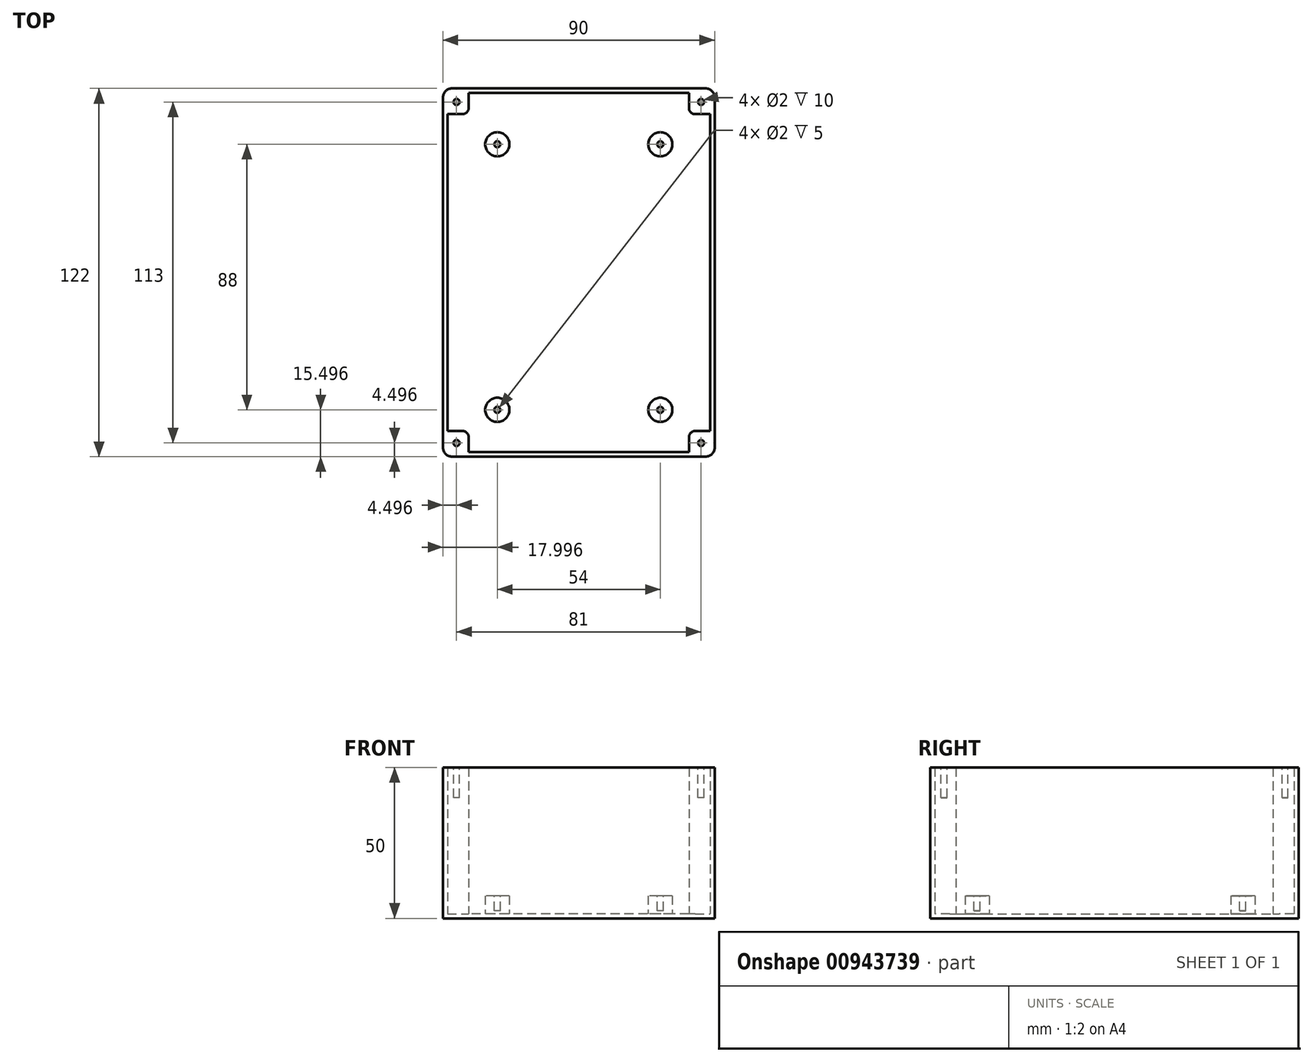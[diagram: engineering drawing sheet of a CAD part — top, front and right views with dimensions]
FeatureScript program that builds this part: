
annotation { "Feature Type Name" : "Feature", "Feature Type Description" : "" }
export const myFeature = defineFeature(function(context is Context, id is Id, definition is map)
    precondition{}
    {
        {
            var Q0;
            Q0=qCreatedBy(makeId("Top.planeOp"),FACE);
            var sketch = newSketch(context, id + "F0", { "sketchPlane" : qUnion([Q0])});
            skLineSegment(sketch, "E0.bottom", {"start": v(44.35, -58.9) * mm, "end": v(-39.65, -58.9) * mm});
            skLineSegment(sketch, "E0.top", {"start": v(44.35, 63.1) * mm, "end": v(-39.65, 63.1) * mm});
            skLineSegment(sketch, "E0.left", {"start": v(47.35, -55.9) * mm, "end": v(47.35, 60.1) * mm});
            skLineSegment(sketch, "E0.right", {"start": v(-42.65, -55.9) * mm, "end": v(-42.65, 60.1) * mm});
            skPoint(sketch, "E1", {"position": v(2.35, 63.1) * mm});
            skPoint(sketch, "E2.visualSharp", {"position": v(47.35, 63.1) * mm});
            skArc(sketch, "E2.filletArc", {"start": v(47.35, 60.1) * mm, "mid": v(46.47, 62.23) * mm, "end": v(44.35, 63.1) * mm});
            skPoint(sketch, "E3.visualSharp", {"position": v(-42.65, 63.1) * mm});
            skArc(sketch, "E3.filletArc", {"start": v(-39.65, 63.1) * mm, "mid": v(-41.78, 62.23) * mm, "end": v(-42.65, 60.1) * mm});
            skPoint(sketch, "E4.visualSharp", {"position": v(-42.65, -58.9) * mm});
            skArc(sketch, "E4.filletArc", {"start": v(-42.65, -55.9) * mm, "mid": v(-41.78, -58.02) * mm, "end": v(-39.65, -58.9) * mm});
            skPoint(sketch, "E5.visualSharp", {"position": v(47.35, -58.9) * mm});
            skArc(sketch, "E5.filletArc", {"start": v(44.35, -58.9) * mm, "mid": v(46.47, -58.02) * mm, "end": v(47.35, -55.9) * mm});
            skSolve(sketch);
        }
        {
            var Q0;
            Q0 = qSketchRegion(id + "F0", true);
            extrude(context, id + "F1", {"entities" : qUnion([Q0]), "depth" : 50 * mm, "offsetDistance" : 25 * mm});
        }
        {
            var Q0;
            Q0=makeQuery(id+"F1.opExtrude","CAP_FACE",FACE,{"disambiguationData":[OSD([sQuery(id+"F0.wireOp",EDGE,"E0.bottom"),sQuery(id+"F0.wireOp",EDGE,"E0.top"),sQuery(id+"F0.wireOp",EDGE,"E0.left"),sQuery(id+"F0.wireOp",EDGE,"E0.right"),sQuery(id+"F0.wireOp",EDGE,"E2.filletArc"),sQuery(id+"F0.wireOp",EDGE,"E3.filletArc"),sQuery(id+"F0.wireOp",EDGE,"E4.filletArc"),sQuery(id+"F0.wireOp",EDGE,"E5.filletArc")])],"isStart":false});
            shell(context, id + "F2", {"entities" : qUnion([Q0]), "thickness" : 1.5 * mm});
        }
        {
            var Q0;
            Q0=makeQuery(id+"F2.opShell","OFFSET_FACE",FACE,{"disambiguationData":[OSD([sQuery(id+"F0.wireOp",EDGE,"E0.bottom"),sQuery(id+"F0.wireOp",EDGE,"E0.top"),sQuery(id+"F0.wireOp",EDGE,"E0.left"),sQuery(id+"F0.wireOp",EDGE,"E0.right"),sQuery(id+"F0.wireOp",EDGE,"E2.filletArc"),sQuery(id+"F0.wireOp",EDGE,"E3.filletArc"),sQuery(id+"F0.wireOp",EDGE,"E4.filletArc"),sQuery(id+"F0.wireOp",EDGE,"E5.filletArc")])]});
            var sketch = newSketch(context, id + "F3", { "sketchPlane" : qUnion([Q0])});
            skLineSegment(sketch, "E6.bottom", {"start": v(-41.15, 61.6) * mm, "end": v(-34.15, 61.6) * mm});
            skLineSegment(sketch, "E6.top", {"start": v(-41.15, 54.6) * mm, "end": v(-36.15, 54.6) * mm});
            skLineSegment(sketch, "E6.left", {"start": v(-41.15, 61.6) * mm, "end": v(-41.15, 54.6) * mm});
            skLineSegment(sketch, "E6.right", {"start": v(-34.15, 61.6) * mm, "end": v(-34.15, 56.6) * mm});
            skLineSegment(sketch, "E7.bottom", {"start": v(-41.15, -50.4) * mm, "end": v(-36.15, -50.4) * mm});
            skLineSegment(sketch, "E7.top", {"start": v(-41.15, -57.4) * mm, "end": v(-34.15, -57.4) * mm});
            skLineSegment(sketch, "E7.left", {"start": v(-41.15, -50.4) * mm, "end": v(-41.15, -57.4) * mm});
            skLineSegment(sketch, "E7.right", {"start": v(-34.15, -52.4) * mm, "end": v(-34.15, -57.4) * mm});
            skLineSegment(sketch, "E8.bottom", {"start": v(40.85, -50.4) * mm, "end": v(45.85, -50.4) * mm});
            skLineSegment(sketch, "E8.top", {"start": v(38.85, -57.4) * mm, "end": v(45.85, -57.4) * mm});
            skLineSegment(sketch, "E8.left", {"start": v(38.85, -52.4) * mm, "end": v(38.85, -57.4) * mm});
            skLineSegment(sketch, "E8.right", {"start": v(45.85, -50.4) * mm, "end": v(45.85, -57.4) * mm});
            skLineSegment(sketch, "E9.bottom", {"start": v(38.85, 61.6) * mm, "end": v(45.85, 61.6) * mm});
            skLineSegment(sketch, "E9.top", {"start": v(40.85, 54.6) * mm, "end": v(45.85, 54.6) * mm});
            skLineSegment(sketch, "E9.left", {"start": v(38.85, 61.6) * mm, "end": v(38.85, 56.6) * mm});
            skLineSegment(sketch, "E9.right", {"start": v(45.85, 61.6) * mm, "end": v(45.85, 54.6) * mm});
            skPoint(sketch, "E10.visualSharp", {"position": v(-34.15, 54.6) * mm});
            skArc(sketch, "E10.filletArc", {"start": v(-36.15, 54.6) * mm, "mid": v(-34.74, 55.2) * mm, "end": v(-34.15, 56.6) * mm});
            skPoint(sketch, "E11.visualSharp", {"position": v(38.85, 54.6) * mm});
            skArc(sketch, "E11.filletArc", {"start": v(38.85, 56.6) * mm, "mid": v(39.43, 55.2) * mm, "end": v(40.85, 54.6) * mm});
            skPoint(sketch, "E12.visualSharp", {"position": v(38.85, -50.4) * mm});
            skArc(sketch, "E12.filletArc", {"start": v(40.85, -50.4) * mm, "mid": v(39.43, -50.98) * mm, "end": v(38.85, -52.4) * mm});
            skPoint(sketch, "E13.visualSharp", {"position": v(-34.15, -50.4) * mm});
            skArc(sketch, "E13.filletArc", {"start": v(-34.15, -52.4) * mm, "mid": v(-34.74, -50.98) * mm, "end": v(-36.15, -50.4) * mm});
            skSolve(sketch);
        }
        {
            var Q0;
            {var subQ1=sQuery(id+"F3.wireOp",EDGE,"E9.top");Q0=makeQuery(id+"F3.imprint","IMPRINT",FACE,{"disambiguationData":[TD([[makeQuery(id+"F3.imprint","IMPRINT",EDGE,{"derivedFrom":subQ1}),1.0]])]});}
            var Q1;
            {var subQ4=sQuery(id+"F3.wireOp",EDGE,"E6.top");Q1=makeQuery(id+"F3.imprint","IMPRINT",FACE,{"disambiguationData":[TD([[makeQuery(id+"F3.imprint","IMPRINT",EDGE,{"derivedFrom":subQ4}),1.0]])]});}
            var Q2;
            {var subQ3=sQuery(id+"F3.wireOp",EDGE,"E7.bottom");Q2=makeQuery(id+"F3.imprint","IMPRINT",FACE,{"disambiguationData":[TD([[makeQuery(id+"F3.imprint","IMPRINT",EDGE,{"derivedFrom":subQ3}),-1.0]])]});}
            var Q3;
            {var subQ3=sQuery(id+"F3.wireOp",EDGE,"E8.bottom");Q3=makeQuery(id+"F3.imprint","IMPRINT",FACE,{"disambiguationData":[TD([[makeQuery(id+"F3.imprint","IMPRINT",EDGE,{"derivedFrom":subQ3}),-1.0]])]});}
            extrude(context, id + "F4", {"entities" : qUnion([Q0, Q1, Q2, Q3]), "operationType" : NewBodyOperationType.ADD, "depth" : 48.5 * mm, "offsetDistance" : 25 * mm});
        }
        {
            var Q0;
            {var subQ0=sQuery(id+"F0.wireOp",EDGE,"E2.filletArc");var subQ1=sQuery(id+"F0.wireOp",EDGE,"E5.filletArc");var subQ2=sQuery(id+"F0.wireOp",EDGE,"E4.filletArc");var subQ3=sQuery(id+"F0.wireOp",EDGE,"E3.filletArc");Q0=makeQuery(id+"F4.boolean.opBoolean","MERGE",FACE,{"derivedFrom":[makeQuery(id+"F1.opExtrude","CAP_FACE",FACE,{"disambiguationData":[OSD([sQuery(id+"F0.wireOp",EDGE,"E0.bottom"),sQuery(id+"F0.wireOp",EDGE,"E0.top"),sQuery(id+"F0.wireOp",EDGE,"E0.left"),sQuery(id+"F0.wireOp",EDGE,"E0.right"),subQ0,subQ3,subQ2,subQ1])],"isStart":false}),makeQuery(id+"F4.opExtrude","CAP_FACE",FACE,{"disambiguationData":[OSD([subQ3,sQuery(id+"F3.wireOp",EDGE,"E6.bottom"),sQuery(id+"F3.wireOp",EDGE,"E6.top"),sQuery(id+"F3.wireOp",EDGE,"E6.left"),sQuery(id+"F3.wireOp",EDGE,"E6.right")])],"isStart":false}),makeQuery(id+"F4.opExtrude","CAP_FACE",FACE,{"disambiguationData":[OSD([subQ2,sQuery(id+"F3.wireOp",EDGE,"E7.bottom"),sQuery(id+"F3.wireOp",EDGE,"E7.top"),sQuery(id+"F3.wireOp",EDGE,"E7.left"),sQuery(id+"F3.wireOp",EDGE,"E7.right")])],"isStart":false}),makeQuery(id+"F4.opExtrude","CAP_FACE",FACE,{"disambiguationData":[OSD([subQ1,sQuery(id+"F3.wireOp",EDGE,"E8.bottom"),sQuery(id+"F3.wireOp",EDGE,"E8.top"),sQuery(id+"F3.wireOp",EDGE,"E8.left"),sQuery(id+"F3.wireOp",EDGE,"E8.right")])],"isStart":false}),makeQuery(id+"F4.opExtrude","CAP_FACE",FACE,{"disambiguationData":[OSD([subQ0,sQuery(id+"F3.wireOp",EDGE,"E9.bottom"),sQuery(id+"F3.wireOp",EDGE,"E9.top"),sQuery(id+"F3.wireOp",EDGE,"E9.left"),sQuery(id+"F3.wireOp",EDGE,"E9.right")])],"isStart":false})]});}
            var sketch = newSketch(context, id + "F5", { "sketchPlane" : qUnion([Q0])});
            skCircle(sketch, "E14", {"center": v(42.85, 58.6) * mm, "radius": 1 * mm});
            skCircle(sketch, "E15", {"center": v(-38.15, 58.6) * mm, "radius": 1 * mm});
            skCircle(sketch, "E16", {"center": v(-38.15, -54.4) * mm, "radius": 1 * mm});
            skCircle(sketch, "E17", {"center": v(42.85, -54.4) * mm, "radius": 1 * mm});
            skSolve(sketch);
        }
        {
            var Q0;
            Q0=makeQuery(id+"F5.imprint","IMPRINT",FACE,{"disambiguationData":[TD([[makeQuery(id+"F5.imprint","IMPRINT",EDGE,{"derivedFrom":sQuery(id+"F5.wireOp",EDGE,"E17")}),1.0]])]});
            var Q1;
            Q1=makeQuery(id+"F5.imprint","IMPRINT",FACE,{"disambiguationData":[TD([[makeQuery(id+"F5.imprint","IMPRINT",EDGE,{"derivedFrom":sQuery(id+"F5.wireOp",EDGE,"E16")}),1.0]])]});
            var Q2;
            Q2=makeQuery(id+"F5.imprint","IMPRINT",FACE,{"disambiguationData":[TD([[makeQuery(id+"F5.imprint","IMPRINT",EDGE,{"derivedFrom":sQuery(id+"F5.wireOp",EDGE,"E15")}),1.0]])]});
            var Q3;
            Q3=makeQuery(id+"F5.imprint","IMPRINT",FACE,{"disambiguationData":[TD([[makeQuery(id+"F5.imprint","IMPRINT",EDGE,{"derivedFrom":sQuery(id+"F5.wireOp",EDGE,"E14")}),1.0]])]});
            extrude(context, id + "F6", {"entities" : qUnion([Q0, Q1, Q2, Q3]), "operationType" : NewBodyOperationType.REMOVE, "oppositeDirection" : true, "depth" : 10 * mm, "offsetDistance" : 25 * mm});
        }
        {
            var Q0;
            Q0=makeQuery(id+"F2.opShell","OFFSET_FACE",FACE,{"disambiguationData":[OSD([sQuery(id+"F0.wireOp",EDGE,"E0.bottom"),sQuery(id+"F0.wireOp",EDGE,"E0.top"),sQuery(id+"F0.wireOp",EDGE,"E0.left"),sQuery(id+"F0.wireOp",EDGE,"E0.right"),sQuery(id+"F0.wireOp",EDGE,"E2.filletArc"),sQuery(id+"F0.wireOp",EDGE,"E3.filletArc"),sQuery(id+"F0.wireOp",EDGE,"E4.filletArc"),sQuery(id+"F0.wireOp",EDGE,"E5.filletArc")])]});
            var sketch = newSketch(context, id + "F7", { "sketchPlane" : qUnion([Q0])});
            skCircle(sketch, "E18", {"center": v(-24.65, 44.6) * mm, "radius": 4 * mm});
            skCircle(sketch, "E19", {"center": v(29.35, 44.6) * mm, "radius": 4 * mm});
            skCircle(sketch, "E20", {"center": v(-24.65, -43.4) * mm, "radius": 4 * mm});
            skCircle(sketch, "E21", {"center": v(29.35, -43.4) * mm, "radius": 4 * mm});
            skSolve(sketch);
        }
        {
            var Q0;
            Q0=makeQuery(id+"F7.imprint","IMPRINT",FACE,{"disambiguationData":[TD([[makeQuery(id+"F7.imprint","IMPRINT",EDGE,{"derivedFrom":sQuery(id+"F7.wireOp",EDGE,"E19")}),1.0]])]});
            var Q1;
            Q1=makeQuery(id+"F7.imprint","IMPRINT",FACE,{"disambiguationData":[TD([[makeQuery(id+"F7.imprint","IMPRINT",EDGE,{"derivedFrom":sQuery(id+"F7.wireOp",EDGE,"E20")}),1.0]])]});
            var Q2;
            Q2=makeQuery(id+"F7.imprint","IMPRINT",FACE,{"disambiguationData":[TD([[makeQuery(id+"F7.imprint","IMPRINT",EDGE,{"derivedFrom":sQuery(id+"F7.wireOp",EDGE,"E21")}),1.0]])]});
            var Q3;
            Q3=makeQuery(id+"F7.imprint","IMPRINT",FACE,{"disambiguationData":[TD([[makeQuery(id+"F7.imprint","IMPRINT",EDGE,{"derivedFrom":sQuery(id+"F7.wireOp",EDGE,"E18")}),1.0]])]});
            extrude(context, id + "F8", {"entities" : qUnion([Q0, Q1, Q2, Q3]), "operationType" : NewBodyOperationType.ADD, "depth" : 6 * mm, "offsetDistance" : 25 * mm});
        }
        {
            var Q0;
            Q0=makeQuery(id+"F8.opExtrude","CAP_FACE",FACE,{"disambiguationData":[OSD([sQuery(id+"F7.wireOp",EDGE,"E18")])],"isStart":false});
            var sketch = newSketch(context, id + "F9", { "sketchPlane" : qUnion([Q0])});
            skCircle(sketch, "E22.0", {"center": v(-24.65, 44.6) * mm, "radius": 1 * mm});
            skCircle(sketch, "E23.0", {"center": v(29.35, 44.6) * mm, "radius": 1 * mm});
            skCircle(sketch, "E24.0", {"center": v(-24.65, -43.4) * mm, "radius": 1 * mm});
            skCircle(sketch, "E25.0", {"center": v(29.35, -43.4) * mm, "radius": 1 * mm});
            skSolve(sketch);
        }
        {
            var Q0;
            Q0=makeQuery(id+"F9.imprint","IMPRINT",FACE,{"disambiguationData":[TD([[makeQuery(id+"F9.imprint","IMPRINT",EDGE,{"derivedFrom":sQuery(id+"F9.wireOp",EDGE,"E23.0")}),1.0]])]});
            var Q1;
            Q1=makeQuery(id+"F9.imprint","IMPRINT",FACE,{"disambiguationData":[TD([[makeQuery(id+"F9.imprint","IMPRINT",EDGE,{"derivedFrom":sQuery(id+"F9.wireOp",EDGE,"E24.0")}),1.0]])]});
            var Q2;
            Q2=makeQuery(id+"F9.imprint","IMPRINT",FACE,{"disambiguationData":[TD([[makeQuery(id+"F9.imprint","IMPRINT",EDGE,{"derivedFrom":sQuery(id+"F9.wireOp",EDGE,"E25.0")}),1.0]])]});
            var Q3;
            Q3=makeQuery(id+"F9.imprint","IMPRINT",FACE,{"disambiguationData":[TD([[makeQuery(id+"F9.imprint","IMPRINT",EDGE,{"derivedFrom":sQuery(id+"F9.wireOp",EDGE,"E22.0")}),1.0]])]});
            extrude(context, id + "F10", {"entities" : qUnion([Q0, Q1, Q2, Q3]), "operationType" : NewBodyOperationType.REMOVE, "oppositeDirection" : true, "depth" : 5 * mm, "offsetDistance" : 25 * mm});
        }
    });
